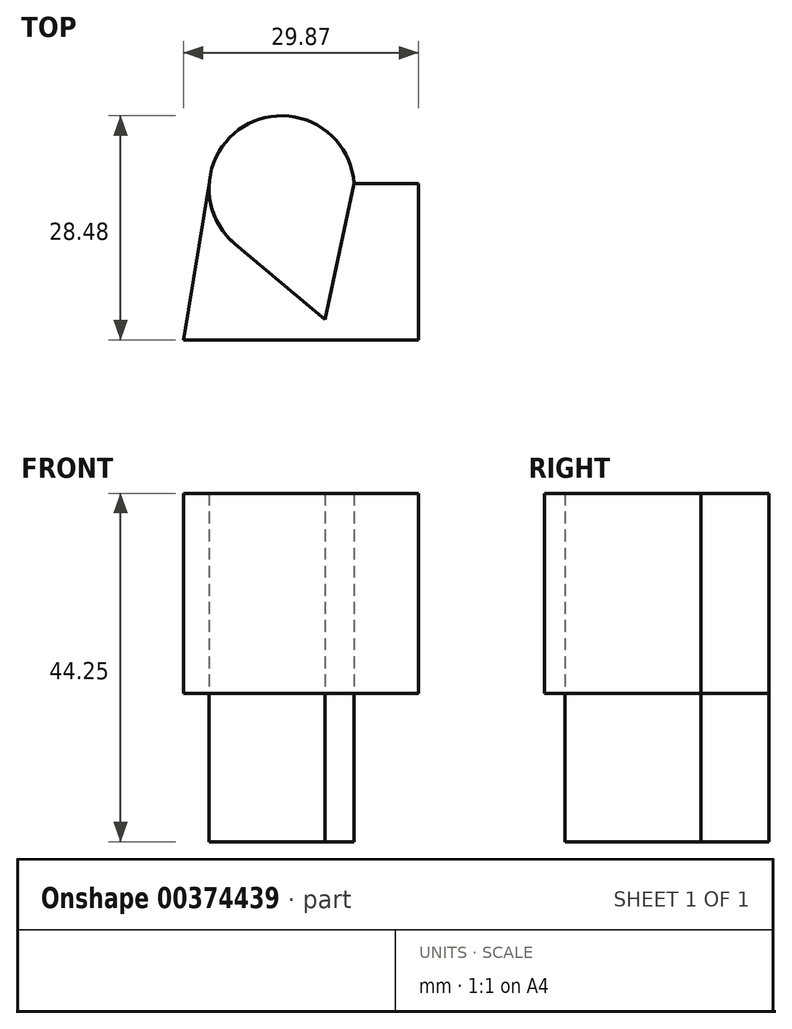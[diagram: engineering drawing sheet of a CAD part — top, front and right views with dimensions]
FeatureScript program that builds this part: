
annotation { "Feature Type Name" : "Feature", "Feature Type Description" : "" }
export const myFeature = defineFeature(function(context is Context, id is Id, definition is map)
    precondition{}
    {
        {
            var Q0;
            Q0=qCreatedBy(makeId("Top.planeOp"),FACE);
            var sketch = newSketch(context, id + "F0", { "sketchPlane" : qUnion([Q0])});
            skArc(sketch, "E0", {"start": v(-3.18, 10.1) * mm, "mid": v(-16.56, 17.7) * mm, "end": v(-18.3, 2.41) * mm});
            skLineSegment(sketch, "E1", {"start": v(-18.3, 2.41) * mm, "end": v(-6.88, -7.16) * mm});
            skLineSegment(sketch, "E2", {"start": v(-6.88, -7.16) * mm, "end": v(-3.18, 10.1) * mm});
            skSolve(sketch);
        }
        {
            var Q0;
            Q0=makeQuery(id+"F0.imprint","IMPRINT",FACE,{"disambiguationData":[TD([[makeQuery(id+"F0.imprint","IMPRINT",EDGE,{"derivedFrom":sQuery(id+"F0.wireOp",EDGE,"E0")}),1.0]])]});
            var Q1;
            Q1=sQuery(id+"F0.wireOp",EDGE,"E2");
            var Q2;
            Q2=sQuery(id+"F0.wireOp",EDGE,"E0");
            var Q3;
            Q3=sQuery(id+"F0.wireOp",EDGE,"E1");
            extrude(context, id + "F1", {"entities" : qUnion([Q0]), "surfaceEntities" : qUnion([Q1, Q2, Q3]), "depth" : 18.85 * mm});
        }
        {
            var Q0;
            Q0=makeQuery(id+"F1.opExtrude","CAP_FACE",FACE,{"disambiguationData":[OSD([sQuery(id+"F0.wireOp",EDGE,"E0"),sQuery(id+"F0.wireOp",EDGE,"E1"),sQuery(id+"F0.wireOp",EDGE,"E2")])],"isStart":false});
            var sketch = newSketch(context, id + "F2", { "sketchPlane" : qUnion([Q0])});
            skLineSegment(sketch, "E3", {"start": v(-3.18, 10.1) * mm, "end": v(5.02, 10.1) * mm});
            skLineSegment(sketch, "E4", {"start": v(5.02, 10.1) * mm, "end": v(5.02, -9.78) * mm});
            skLineSegment(sketch, "E5", {"start": v(5.02, -9.78) * mm, "end": v(-24.85, -9.78) * mm});
            skLineSegment(sketch, "E6", {"start": v(-24.85, -9.78) * mm, "end": v(-21.59, 9.99) * mm});
            skSolve(sketch);
        }
        {
            var Q0;
            Q0=makeQuery(id+"F2.imprint","IMPRINT",FACE,{"disambiguationData":[TD([[makeQuery(id+"F2.imprint","IMPRINT",EDGE,{"derivedFrom":sQuery(id+"F2.wireOp",EDGE,"E3")}),-1.0]])]});
            extrude(context, id + "F3", {"entities" : qUnion([Q0]), "depth" : 25.4 * mm});
        }
        {
            var Q0;
            Q0=makeQuery(id+"F1.opExtrude","CAP_FACE",FACE,{"disambiguationData":[OSD([sQuery(id+"F0.wireOp",EDGE,"E0"),sQuery(id+"F0.wireOp",EDGE,"E1"),sQuery(id+"F0.wireOp",EDGE,"E2")])],"isStart":false});
            extrude(context, id + "F4", {"entities" : qUnion([Q0]), "depth" : 25.4 * mm});
        }
    });
